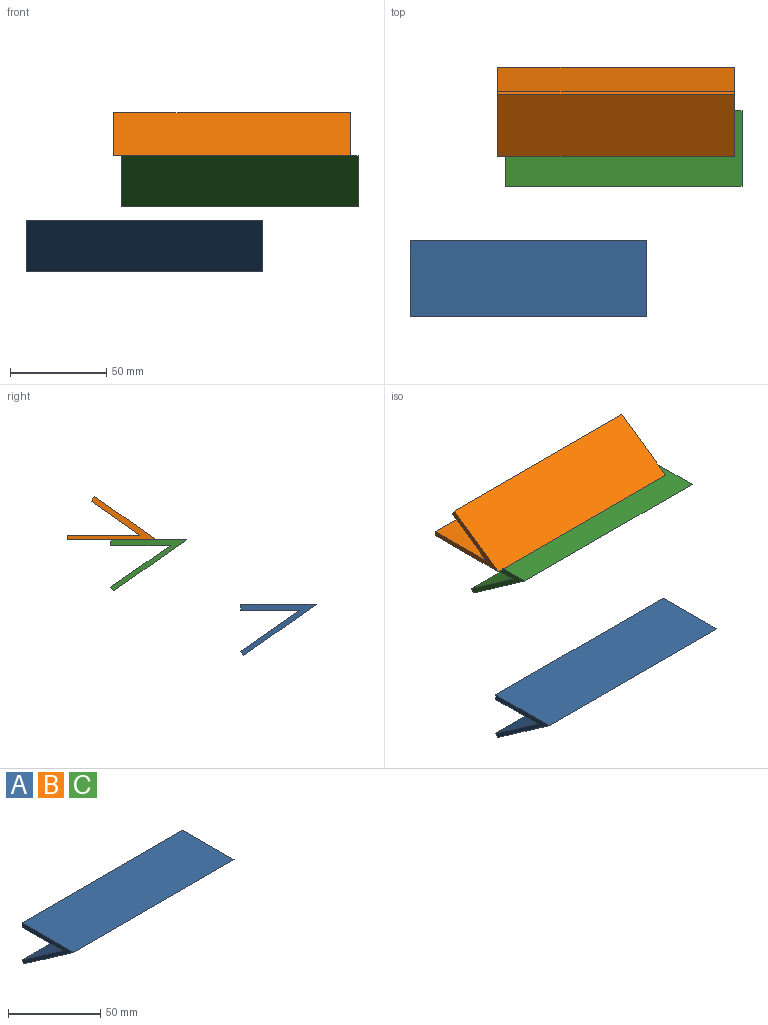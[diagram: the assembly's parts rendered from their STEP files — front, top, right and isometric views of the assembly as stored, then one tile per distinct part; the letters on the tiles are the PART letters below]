
ASSEMBLY  parts=3 mates=1
PART A: 8 faces, bbox 123x39.3x26.5 mm
  f0: plane 123x3mm, normal (0,1,0), area 369mm2, adj f1,f2,f3,f4
  f1: plane 123x39.28mm, normal (0,0,1), area 4832mm2, adj f0,f3,f4,f5
  f2: plane 123x30.72mm, normal (0,0,-1), area 3778mm2, adj f0,f3,f4,f6
  f3: plane 39.28x26.52mm, normal (1,0,0), area 207.9mm2, adj f0,f1,f2,f5,f6,f7
  f4: plane 39.28x26.52mm, normal (-1,0,0), area 207.9mm2, adj f0,f1,f2,f5,f6,f7
  f5: plane 123x37.88mm, normal (0,-0.57,-0.82), area 5687.1mm2, adj f1,f3,f4,f7
  f6: plane 123x30.72mm, normal (0,0.57,0.82), area 4612.1mm2, adj f2,f3,f4,f7
  f7: plane 123x2.01mm, normal (0,0.82,-0.57), area 302.3mm2, adj f3,f4,f5,f6
PART B: same geometry as A
PART C: same geometry as A
PLACE A t=(-61.44,-17.34,-15.24)mm
PLACE B rot(axis=(1,0,0),35deg) t=(-15.84,60.37,41.36)mm
PLACE C t=(-12,50.16,18.28)mm
MATE planar B.f5 <-> C.f1  axis (0,0,-1) through (45.66,49.58,21.28)mm
